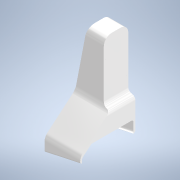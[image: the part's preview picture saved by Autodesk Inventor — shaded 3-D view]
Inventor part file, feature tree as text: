
AUTODESK INVENTOR PART (.ipt)
format: ipt  version: 2021 (Build 250183000, 183)  size: 265,728 bytes
history: native  units: mm
features: sketch x8, extrude x7, fillet x4, shell x1, hole x1
ambient origin geometry x8: Origin, YZ Plane, XZ Plane, XY Plane, X Axis, Y Axis, Z Axis, Center Point
bodies: Solid1 (feature_tree)
feature tree (21):
  extrude  "Extrusion1"  Depth=1400.0mm
  extrude  "Extrusion2"  Depth=450.0mm
  extrude  "Extrusion3"  Depth=180.0mm
  fillet  "Fillet5"  Radius=430.0mm
  fillet  "Fillet6"  Radius=180.0mm
  extrude  "Extrusion7"  Depth=100.0mm
  fillet  "Fillet7"  Radius=1000.0mm
  shell  "Shell2"  Thickness=100.0mm
  extrude  "Extrusion8"  Depth=200.0mm
  extrude  "Extrusion9"  Depth=50.0mm TaperAngle=0.0deg
  fillet  "Fillet8"  Radius=50.0mm
  hole  "Hole1"  [1 undecoded]
  extrude  "Extrusion10"  Depth=10.0mm
  sketch  "Sketch1"  dims[d0=900.0mm d1=1400.0mm]
  sketch  "Sketch8"  dims[d2=700.0mm d3=450.0mm]
  sketch  "Sketch9"  dims[d4=1000.0mm d5=0.0mm d6=1500.0mm d7=430.0mm d8=180.0mm]
  sketch  "Sketch16"  dims[d9=620.0mm d10=0.0mm d11=6.981317mm d12=1000.0mm d13=0.0mm d28=100.0mm]
  sketch  "Sketch18"  dims[d29=200.0mm d30=2.094395mm]
  sketch  "Sketch19"  dims[d31=1100.0mm d32=1500.0mm d33=0.0mm d34=50.0mm]
  sketch  "Sketch20"  dims[d35=2.0mm d39=50.0mm]
  sketch  "Sketch21"  dims[d40=50.0mm d41=6.0mm d42=300.0mm d43=0.0mm d44=200.0mm d45=300.0mm d46=0.0mm d47=50.0mm d48=210.0mm d49=460.0mm d50=10.0mm d51=6.0mm d52=4.0mm d53=2.0mm d54=90.0deg d55=8.0mm d56=20.594885mm d57=6.981317mm d64=10.0mm d65=10.0mm d66=10.0mm d68=12.0mm d69=0.0mm d71=817.0mm d75=40.0mm]
note: 1 required parameter value undecoded (feature->parameter linkage not recoverable at this tier; creation-order binding heuristic only, values carry confidence <= 0.55)
